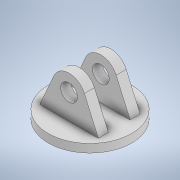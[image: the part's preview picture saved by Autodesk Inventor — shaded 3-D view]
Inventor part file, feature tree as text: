
AUTODESK INVENTOR PART (.ipt)
format: ipt  version: 2021 (Build 250183000, 183)  size: 134,144 bytes
history: native  units: in
note: dims shown in document units (in); Inventor stores cm internally (conversion verified against a paired STEP export)
features: extrude x3, sketch x3, plane x1
ambient origin geometry x8: Origin, YZ Plane, XZ Plane, XY Plane, X Axis, Y Axis, Z Axis, Center Point
bodies: Solid1 (feature_tree)
feature tree (7):
  extrude  "Extrusion1"  Depth=0.0394in TaperAngle=0.0deg
  plane  "Work Plane1"
  extrude  "Extrusion2"  Depth=0.1575in
  extrude  "Extrusion3"  Depth=0.1575in
  sketch  "Sketch1"  dims[d0=0.3937in d1=0.0394in d2=0.0in]
  sketch  "Sketch2"  dims[d3=0.0in d4=0.1575in]
  sketch  "Sketch3"  dims[d5=0.0787in d6=0.1575in d7=0.1378in d8=0.1378in d9=0.1969in d10=0.0in d11=0.1575in d12=0.1024in d13=0.0in]
